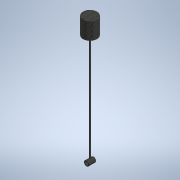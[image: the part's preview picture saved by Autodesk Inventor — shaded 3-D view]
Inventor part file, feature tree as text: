
AUTODESK INVENTOR PART (.ipt)
format: ipt  version: 2020 (Build 240168000, 168)  size: 123,392 bytes
history: native  units: in
note: dims shown in document units (in); Inventor stores cm internally (conversion verified against a paired STEP export)
features: sketch x4, extrude x3, hole x1
ambient origin geometry x8: Origin, YZ Plane, XZ Plane, XY Plane, X Axis, Y Axis, Z Axis, Center Point
bodies: Body1 (feature_tree)
feature tree (8):
  extrude  "Extrusion2"  Depth=7.0866in
  extrude  "Extrusion3"  Depth=9.8425in
  hole  "Hole1"  [1 undecoded]
  extrude  "Extrusion4"  Depth=23.622in TaperAngle=0.0deg
  sketch  "Sketch4"  dims[d14=4.7244in d15=7.0866in]
  sketch  "Sketch6"  dims[d16=9.8425in d17=0.0in d18=1.9685in]
  sketch  "Sketch7"  dims[d19=177.1654in d20=0.0in]
  sketch  "Sketch8"  dims[d21=4.7244in d22=29.5276in d23=14.7638in d24=9.8425in d25=90.0deg d26=39.3701in d27=0.8108in d28=19.685in d29=23.622in d30=0.0in]
note: 1 required parameter value undecoded (feature->parameter linkage not recoverable at this tier; creation-order binding heuristic only, values carry confidence <= 0.55)
